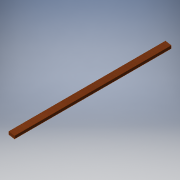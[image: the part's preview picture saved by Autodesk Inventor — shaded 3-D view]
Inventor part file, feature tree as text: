
AUTODESK INVENTOR PART (.ipt)
format: ipt  version: 2016 (Build 200138000, 138)  size: 110,080 bytes
history: native  units: in
note: dims shown in document units (in); Inventor stores cm internally (conversion verified against a paired STEP export)
features: extrude x3, sketch x3
ambient origin geometry x8: Origin, YZ Plane, XZ Plane, XY Plane, X Axis, Y Axis, Z Axis, Center Point
bodies: Solid1 (feature_tree)
feature tree (6):
  extrude  "Extrusion1"  Depth=3.5in
  extrude  "Extrusion3"  Depth=1.5in
  extrude  "Extrusion4"  Depth=1.5in
  sketch  "Sketch1"  dims[d0=82.46in d1=3.5in]
  sketch  "Sketch4"  dims[d2=1.5in d3=0.0in d8=0.0618in]
  sketch  "Sketch5"  dims[d9=1.5in d10=0.0in d11=0.0618in d12=1.5in d13=0.0in]
